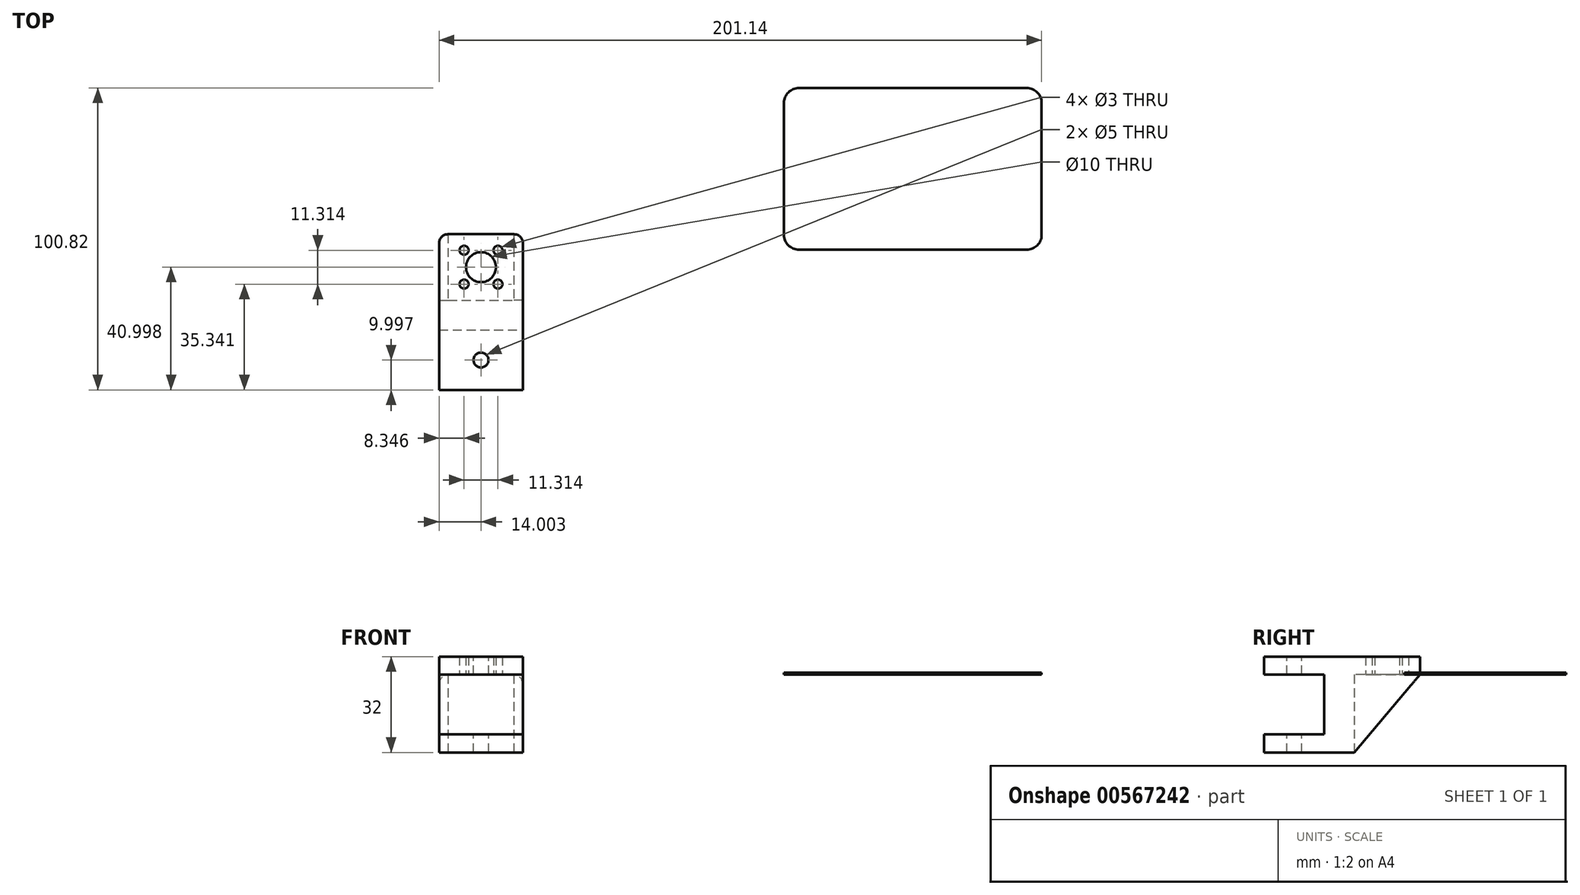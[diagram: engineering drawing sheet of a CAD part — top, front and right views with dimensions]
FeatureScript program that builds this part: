
annotation { "Feature Type Name" : "Feature", "Feature Type Description" : "" }
export const myFeature = defineFeature(function(context is Context, id is Id, definition is map)
    precondition{}
    {
        {
            var Q0;
            Q0=qCreatedBy(makeId("Top.planeOp"),FACE);
            var sketch = newSketch(context, id + "F0", { "sketchPlane" : qUnion([Q0])});
            skLineSegment(sketch, "E0.bottom", {"start": v(-61.67, 27.14) * mm, "end": v(-39.67, 27.14) * mm});
            skLineSegment(sketch, "E0.top", {"start": v(-61.67, 5.14) * mm, "end": v(-39.67, 5.14) * mm});
            skLineSegment(sketch, "E0.left", {"start": v(-61.67, 27.14) * mm, "end": v(-61.67, 5.14) * mm});
            skLineSegment(sketch, "E0.right", {"start": v(-39.67, 27.14) * mm, "end": v(-39.67, 5.14) * mm});
            skPoint(sketch, "E1.centerSnap0", {"position": v(-50.67, 27.14) * mm});
            skPoint(sketch, "E1.centerSnap1", {"position": v(-61.67, 16.14) * mm});
            skCircle(sketch, "E2", {"center": v(-56.32, 21.8) * mm, "radius": 1.5 * mm});
            skCircle(sketch, "E3", {"center": v(-45, 10.48) * mm, "radius": 1.5 * mm});
            skCircle(sketch, "E4", {"center": v(-45, 21.8) * mm, "radius": 1.5 * mm});
            skCircle(sketch, "E5", {"center": v(-56.32, 10.48) * mm, "radius": 1.5 * mm});
            skCircle(sketch, "E6", {"center": v(-50.67, 16.14) * mm, "radius": 5 * mm});
            skSolve(sketch);
        }
        {
            var Q0;
            Q0=makeQuery(id+"F0.imprint","IMPRINT",FACE,{"disambiguationData":[TD([[makeQuery(id+"F0.imprint","IMPRINT",EDGE,{"derivedFrom":sQuery(id+"F0.wireOp",EDGE,"E0.bottom")}),-1.0]])]});
            extrude(context, id + "F1", {"entities" : qUnion([Q0]), "depth" : 6 * mm, "offsetDistance" : 25 * mm});
        }
        {
            var Q0;
            Q0=makeQuery(id+"F1.opExtrude","SWEPT_FACE",FACE,{"disambiguationData":[OSD([sQuery(id+"F0.wireOp",EDGE,"E0.top")])]});
            var sketch = newSketch(context, id + "F2", { "sketchPlane" : qUnion([Q0])});
            skLineSegment(sketch, "E7.bottom", {"start": v(-61.67, 6) * mm, "end": v(-39.67, 6) * mm});
            skLineSegment(sketch, "E7.top", {"start": v(-61.67, -26) * mm, "end": v(-39.67, -26) * mm});
            skLineSegment(sketch, "E7.left", {"start": v(-61.67, 6) * mm, "end": v(-61.67, -26) * mm});
            skLineSegment(sketch, "E7.right", {"start": v(-39.67, 6) * mm, "end": v(-39.67, -26) * mm});
            skSolve(sketch);
        }
        {
            var Q0;
            Q0 = qSketchRegion(id + "F2", true);
            extrude(context, id + "F3", {"entities" : qUnion([Q0]), "operationType" : NewBodyOperationType.ADD, "depth" : 10 * mm, "offsetDistance" : 25 * mm});
        }
        {
            var Q0;
            Q0=makeQuery(id+"F3.opExtrude","CAP_FACE",FACE,{"disambiguationData":[OSD([sQuery(id+"F2.wireOp",EDGE,"E7.bottom"),sQuery(id+"F2.wireOp",EDGE,"E7.top"),sQuery(id+"F2.wireOp",EDGE,"E7.left"),sQuery(id+"F2.wireOp",EDGE,"E7.right")])],"isStart":false});
            var sketch = newSketch(context, id + "F4", { "sketchPlane" : qUnion([Q0])});
            skLineSegment(sketch, "E8", {"start": v(-61.67, 0) * mm, "end": v(-39.67, 0) * mm});
            skLineSegment(sketch, "E9", {"start": v(-61.67, -20) * mm, "end": v(-39.67, -20) * mm});
            skSolve(sketch);
        }
        {
            var Q0;
            {var subQ0=sQuery(id+"F4.wireOp",EDGE,"E8");Q0=makeQuery(id+"F4.imprint","IMPRINT",FACE,{"disambiguationData":[TD([[makeQuery(id+"F4.imprint","IMPRINT",EDGE,{"derivedFrom":subQ0}),1.0]])]});}
            var Q1;
            {var subQ0=sQuery(id+"F4.wireOp",EDGE,"E9");Q1=makeQuery(id+"F4.imprint","IMPRINT",FACE,{"disambiguationData":[TD([[makeQuery(id+"F4.imprint","IMPRINT",EDGE,{"derivedFrom":subQ0}),-1.0]])]});}
            extrude(context, id + "F5", {"entities" : qUnion([Q0, Q1]), "operationType" : NewBodyOperationType.ADD, "depth" : 20 * mm, "offsetDistance" : 25 * mm});
        }
        {
            var Q0;
            {var subQ0=sQuery(id+"F2.wireOp",EDGE,"E7.bottom");Q0=makeQuery(id+"F5.boolean.opBoolean","MERGE",FACE,{"derivedFrom":[makeQuery(id+"F3.boolean.opBoolean","MERGE",FACE,{"derivedFrom":[makeQuery(id+"F1.opExtrude","CAP_FACE",FACE,{"disambiguationData":[OSD([sQuery(id+"F0.wireOp",EDGE,"E0.bottom"),sQuery(id+"F0.wireOp",EDGE,"E0.top"),sQuery(id+"F0.wireOp",EDGE,"E0.left"),sQuery(id+"F0.wireOp",EDGE,"E0.right"),sQuery(id+"F0.wireOp",EDGE,"E2"),sQuery(id+"F0.wireOp",EDGE,"E3"),sQuery(id+"F0.wireOp",EDGE,"E4"),sQuery(id+"F0.wireOp",EDGE,"E5"),sQuery(id+"F0.wireOp",EDGE,"E6")])],"isStart":false}),makeQuery(id+"F3.opExtrude","SWEPT_FACE",FACE,{"disambiguationData":[OSD([subQ0])]})]}),makeQuery(id+"F5.opExtrude","SWEPT_FACE",FACE,{"disambiguationData":[OSD([subQ0])]})]});}
            var sketch = newSketch(context, id + "F6", { "sketchPlane" : qUnion([Q0])});
            skCircle(sketch, "E10", {"center": v(-50.67, -14.86) * mm, "radius": 2.5 * mm});
            skPoint(sketch, "E10.centerSnap0", {"position": v(-50.67, -24.86) * mm});
            skSolve(sketch);
        }
        {
            var Q0;
            Q0=makeQuery(id+"F6.imprint","IMPRINT",FACE,{"disambiguationData":[TD([[makeQuery(id+"F6.imprint","IMPRINT",EDGE,{"derivedFrom":sQuery(id+"F6.wireOp",EDGE,"E10")}),1.0]])]});
            extrude(context, id + "F7", {"entities" : qUnion([Q0]), "operationType" : NewBodyOperationType.REMOVE, "endBound" : BoundingType.THROUGH_ALL, "oppositeDirection" : true, "depth" : 25 * mm, "offsetDistance" : 25 * mm});
        }
        {
            var Q0;
            {var subQ0=sQuery(id+"F2.wireOp",EDGE,"E7.left");var subQ1=makeQuery(id+"F3.opExtrude","CAP_EDGE",EDGE,{"disambiguationData":[OSD([subQ0])],"isStart":false});Q0=makeQuery(id+"F5.boolean.opBoolean","MERGE",FACE,{"derivedFrom":[makeQuery(id+"F3.boolean.opBoolean","MERGE",FACE,{"derivedFrom":[makeQuery(id+"F1.opExtrude","SWEPT_FACE",FACE,{"disambiguationData":[OSD([sQuery(id+"F0.wireOp",EDGE,"E0.left")])]}),makeQuery(id+"F3.opExtrude","SWEPT_FACE",FACE,{"disambiguationData":[OSD([subQ0])]})]}),makeQuery(id+"F5.opExtrude","SWEPT_FACE",FACE,{"disambiguationData":[OSD([subQ0]),TDD([makeQuery(id+"F4.imprint","IMPRINT",EDGE,{"disambiguationData":[TD([[makeQuery(id+"F4.imprint","INTERSECT",VERTEX,{"derivedFrom":[makeQuery(id+"F3.opExtrude","CAP_EDGE",EDGE,{"disambiguationData":[OSD([sQuery(id+"F2.wireOp",EDGE,"E7.bottom")])],"isStart":false}),subQ1]}),-1.0]])],"derivedFrom":subQ1})])]}),makeQuery(id+"F5.opExtrude","SWEPT_FACE",FACE,{"disambiguationData":[OSD([subQ0]),TDD([makeQuery(id+"F4.imprint","IMPRINT",EDGE,{"disambiguationData":[TD([[makeQuery(id+"F4.imprint","INTERSECT",VERTEX,{"derivedFrom":[makeQuery(id+"F3.opExtrude","CAP_EDGE",EDGE,{"disambiguationData":[OSD([sQuery(id+"F2.wireOp",EDGE,"E7.top")])],"isStart":false}),subQ1]}),1.0]])],"derivedFrom":subQ1})])]})]});}
            var sketch = newSketch(context, id + "F8", { "sketchPlane" : qUnion([Q0])});
            skLineSegment(sketch, "E11", {"start": v(-5.14, -26) * mm, "end": v(-27.14, 0) * mm});
            skSolve(sketch);
        }
        {
            var Q0;
            Q0=makeQuery(id+"F8.imprint","IMPRINT",FACE,{"disambiguationData":[TD([[makeQuery(id+"F8.imprint","IMPRINT",EDGE,{"derivedFrom":sQuery(id+"F8.wireOp",EDGE,"E11")}),-1.0]])]});
            var Q1;
            {var subQ2=sQuery(id+"F0.wireOp",EDGE,"E0.left");Q1=makeQuery(id+"F8.imprint","IMPRINT",FACE,{"disambiguationData":[TD([[makeQuery(id+"F8.imprint","IMPRINT",EDGE,{"derivedFrom":makeQuery(id+"F1.opExtrude","CAP_EDGE",EDGE,{"disambiguationData":[OSD([subQ2])],"isStart":true})}),1.0]])]});}
            extrude(context, id + "F9", {"entities" : qUnion([Q0, Q1]), "operationType" : NewBodyOperationType.ADD, "depth" : 3 * mm, "offsetDistance" : 25 * mm});
        }
        {
            var Q0;
            {var subQ0=sQuery(id+"F2.wireOp",EDGE,"E7.right");var subQ1=makeQuery(id+"F3.opExtrude","CAP_EDGE",EDGE,{"disambiguationData":[OSD([subQ0])],"isStart":false});Q0=makeQuery(id+"F5.boolean.opBoolean","MERGE",FACE,{"derivedFrom":[makeQuery(id+"F3.boolean.opBoolean","MERGE",FACE,{"derivedFrom":[makeQuery(id+"F1.opExtrude","SWEPT_FACE",FACE,{"disambiguationData":[OSD([sQuery(id+"F0.wireOp",EDGE,"E0.right")])]}),makeQuery(id+"F3.opExtrude","SWEPT_FACE",FACE,{"disambiguationData":[OSD([subQ0])]})]}),makeQuery(id+"F5.opExtrude","SWEPT_FACE",FACE,{"disambiguationData":[OSD([subQ0]),TDD([makeQuery(id+"F4.imprint","IMPRINT",EDGE,{"disambiguationData":[TD([[makeQuery(id+"F4.imprint","INTERSECT",VERTEX,{"derivedFrom":[makeQuery(id+"F3.opExtrude","CAP_EDGE",EDGE,{"disambiguationData":[OSD([sQuery(id+"F2.wireOp",EDGE,"E7.bottom")])],"isStart":false}),subQ1]}),-1.0]])],"derivedFrom":subQ1})])]}),makeQuery(id+"F5.opExtrude","SWEPT_FACE",FACE,{"disambiguationData":[OSD([subQ0]),TDD([makeQuery(id+"F4.imprint","IMPRINT",EDGE,{"disambiguationData":[TD([[makeQuery(id+"F4.imprint","INTERSECT",VERTEX,{"derivedFrom":[makeQuery(id+"F3.opExtrude","CAP_EDGE",EDGE,{"disambiguationData":[OSD([sQuery(id+"F2.wireOp",EDGE,"E7.top")])],"isStart":false}),subQ1]}),1.0]])],"derivedFrom":subQ1})])]})]});}
            var sketch = newSketch(context, id + "F10", { "sketchPlane" : qUnion([Q0])});
            skLineSegment(sketch, "E12", {"start": v(5.14, -26) * mm, "end": v(27.14, 0) * mm});
            skSolve(sketch);
        }
        {
            var Q0;
            Q0=makeQuery(id+"F10.imprint","IMPRINT",FACE,{"disambiguationData":[TD([[makeQuery(id+"F10.imprint","IMPRINT",EDGE,{"derivedFrom":sQuery(id+"F10.wireOp",EDGE,"E12")}),1.0]])]});
            var Q1;
            {var subQ2=sQuery(id+"F0.wireOp",EDGE,"E0.right");Q1=makeQuery(id+"F10.imprint","IMPRINT",FACE,{"disambiguationData":[TD([[makeQuery(id+"F10.imprint","IMPRINT",EDGE,{"derivedFrom":makeQuery(id+"F1.opExtrude","CAP_EDGE",EDGE,{"disambiguationData":[OSD([subQ2])],"isStart":true})}),-1.0]])]});}
            extrude(context, id + "F11", {"entities" : qUnion([Q0, Q1]), "operationType" : NewBodyOperationType.ADD, "depth" : 3 * mm, "offsetDistance" : 25 * mm});
        }
        {
            var Q0;
            Q0=makeQuery(id+"F9.opExtrude","CAP_EDGE",EDGE,{"disambiguationData":[OSD([sQuery(id+"F0.wireOp",EDGE,"E0.bottom"),sQuery(id+"F0.wireOp",EDGE,"E0.left")])],"isStart":false});
            var Q1;
            Q1=makeQuery(id+"F11.opExtrude","CAP_EDGE",EDGE,{"disambiguationData":[OSD([sQuery(id+"F0.wireOp",EDGE,"E0.bottom"),sQuery(id+"F0.wireOp",EDGE,"E0.right")])],"isStart":false});
            fillet(context, id + "F12", {"entities" : qUnion([Q0, Q1]), "radius" : 3 * mm, "tangentPropagation" : true, "allowEdgeOverflow" : false});
        }
        {
            var Q0;
            Q0=qCreatedBy(makeId("Top.planeOp"), FACE);
            var sketch = newSketch(context, id + "F13", { "sketchPlane" : qUnion([Q0])});
            skLineSegment(sketch, "E13.bottom", {"start": v(55.47, 75.96) * mm, "end": v(131.47, 75.96) * mm});
            skLineSegment(sketch, "E13.top", {"start": v(55.47, 21.96) * mm, "end": v(131.47, 21.96) * mm});
            skLineSegment(sketch, "E13.left", {"start": v(50.47, 70.96) * mm, "end": v(50.47, 26.96) * mm});
            skLineSegment(sketch, "E13.right", {"start": v(136.47, 70.96) * mm, "end": v(136.47, 26.96) * mm});
            skPoint(sketch, "E14.0.visualSharp", {"position": v(50.47, 75.96) * mm});
            skArc(sketch, "E14.0.filletArc", {"start": v(55.47, 75.96) * mm, "mid": v(51.93, 74.5) * mm, "end": v(50.47, 70.96) * mm});
            skPoint(sketch, "E15.0.visualSharp", {"position": v(50.47, 21.96) * mm});
            skArc(sketch, "E15.0.filletArc", {"start": v(50.47, 26.96) * mm, "mid": v(51.93, 23.42) * mm, "end": v(55.47, 21.96) * mm});
            skPoint(sketch, "E16.0.visualSharp", {"position": v(136.47, 21.96) * mm});
            skArc(sketch, "E16.0.filletArc", {"start": v(131.47, 21.96) * mm, "mid": v(135, 23.42) * mm, "end": v(136.47, 26.96) * mm});
            skPoint(sketch, "E16.1.visualSharp", {"position": v(136.47, 75.96) * mm});
            skArc(sketch, "E16.1.filletArc", {"start": v(136.47, 70.96) * mm, "mid": v(135, 74.5) * mm, "end": v(131.47, 75.96) * mm});
            skSolve(sketch);
        }
        {
            var Q0;
            Q0 = qSketchRegion(id + "F13", true);
            extrude(context, id + "F14", {"entities" : qUnion([Q0]), "domain" : OperationDomain.MODEL, "flatOperationType" : FlatOperationType.REMOVE, "depth" : 0.6 * mm, "offsetDistance" : 25 * mm});
        }
    });
